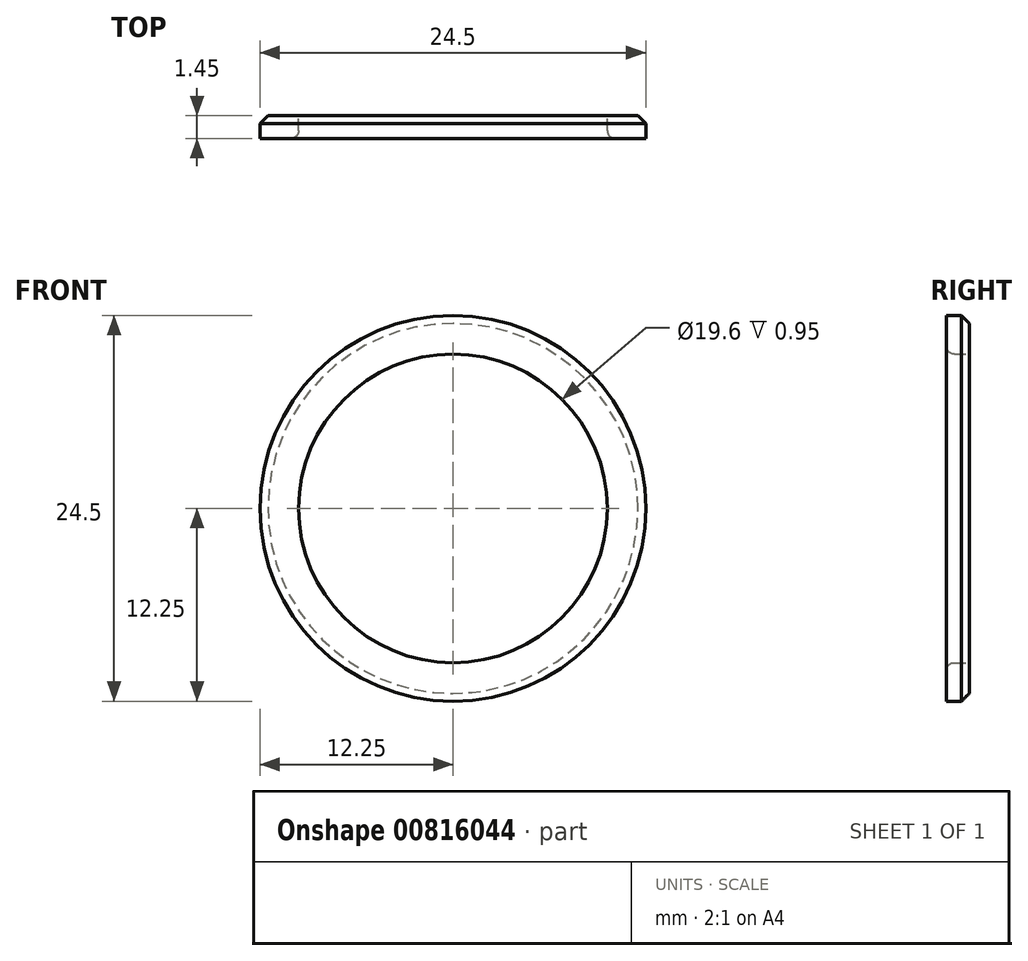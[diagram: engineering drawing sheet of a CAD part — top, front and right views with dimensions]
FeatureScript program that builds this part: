
annotation { "Feature Type Name" : "Feature", "Feature Type Description" : "" }
export const myFeature = defineFeature(function(context is Context, id is Id, definition is map)
    precondition{}
    {
        {
            var Q0;
            Q0=qCreatedBy(makeId("Front.planeOp"),FACE);
            var sketch = newSketch(context, id + "F0", { "sketchPlane" : qUnion([Q0])});
            skCircle(sketch, "E0", {"center": v(0, 0) * mm, "radius": 12.25 * mm});
            skCircle(sketch, "E1", {"center": v(0, 0) * mm, "radius": 9.8 * mm});
            skSolve(sketch);
        }
        {
            var Q0;
            Q0 = qSketchRegion(id + "F0", true);
            extrude(context, id + "F1", {"entities" : qUnion([Q0]), "depth" : 1.45 * mm, "offsetDistance" : 25 * mm});
        }
        {
            var Q0;
            Q0=makeQuery(id+"F1.opExtrude","CAP_EDGE",EDGE,{"disambiguationData":[OSD([sQuery(id+"F0.wireOp",EDGE,"E0")])],"isStart":true});
            chamfer(context, id + "F2", {"entities" : qUnion([Q0]), "width" : 0.5 * mm, "tangentPropagation" : true});
        }
        {
            var Q0;
            Q0=makeQuery(id+"F1.opExtrude","CAP_EDGE",EDGE,{"disambiguationData":[OSD([sQuery(id+"F0.wireOp",EDGE,"E1")])],"isStart":false});
            fillet(context, id + "F3", {"entities" : qUnion([Q0]), "radius" : 0.5 * mm, "tangentPropagation" : true, "allowEdgeOverflow" : false});
        }
    });
